# Revit family: Profim Violle
name_source: partatom
category: Furniture
revit_build: Autodesk Revit Architecture 2015 (Build: 20140322_1515(x64)
units: mm (PartAtom-declared; Revit-internal decimal feet)

## types (1)
- Profim Violle 131SFL
    Armrest Frame material = ProfiM - Violle - Armrest Frame
    Armrest material = ProfiM - Violle - Armrest
    Back Frame material = ProfiM - Violle - Back frame
    Backrest Control material = ProfiM - Violle - Backrest control
    Backrest material = ProfiM - Violle - Backrest
    Base material = ProfiM - Violle - Base
    Damper Lower = ProfiM - Violle - Damper lower
    Damper Lower material = ProfiM - Violle - Damper lower
    Damper Upper material = ProfiM - Violle - Damper upper
    Description = swivel armchair, high backrest, 5-star base on wheels
    Hanger material = ProfiM - Violle - Hanger
    Headrest Frame material = ProfiM - Violle - Headrest Frame
    Headrest material = ProfiM - Violle - Headrest
    Logo material = ProfiM - Violle - logo
    Manufacturer = Profim
    Model = Violle 131SFL
    Seat Frame material = ProfiM - Violle - Seat Frame
    Seat Mechanism material = ProfiM - Violle - Seat Mechanism
    Seat material = ProfiM - Violle - Seat
    Wheels material = ProfiM - Violle - Wheels

## geometry (parser evidence)
native form markers: Sweep x2
no freeform markers — native parametric forms only
